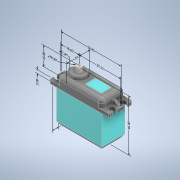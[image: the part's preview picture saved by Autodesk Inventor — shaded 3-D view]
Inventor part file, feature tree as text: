
AUTODESK INVENTOR PART (.ipt)
format: ipt  version: 2022 (Build 260153000, 153)  size: 244,224 bytes
history: mixed  units: mm
features: other x12, fillet x1, imported_body x1
ambient origin geometry x8: Origin, YZ Plane, XZ Plane, XY Plane, X Axis, Y Axis, Z Axis, Center Point
bodies: Solid1 (imported_parasolid)
feature tree (14):
  other  "Annotations"
  fillet  "Fillet8"  [1 undecoded]
  other  "Linear Dimension 3"
  other  "Linear Dimension 4"
  other  "Linear Dimension 5"
  other  "Linear Dimension 6"
  other  "Linear Dimension 7"
  other  "Linear Dimension 8"
  other  "Linear Dimension 9"
  other  "Linear Dimension 10"
  other  "Linear Dimension 11"
  other  "Radial Dimension 1"
  other  "Diameter Dimension 1"
  imported_body  NMx_Import_Brep_tag  [imported B-rep: ~93 faces, bbox_mm=[53.85, 46.0, 20.7]]
note: 1 required parameter value undecoded (feature->parameter linkage not recoverable at this tier; creation-order binding heuristic only, values carry confidence <= 0.55)
